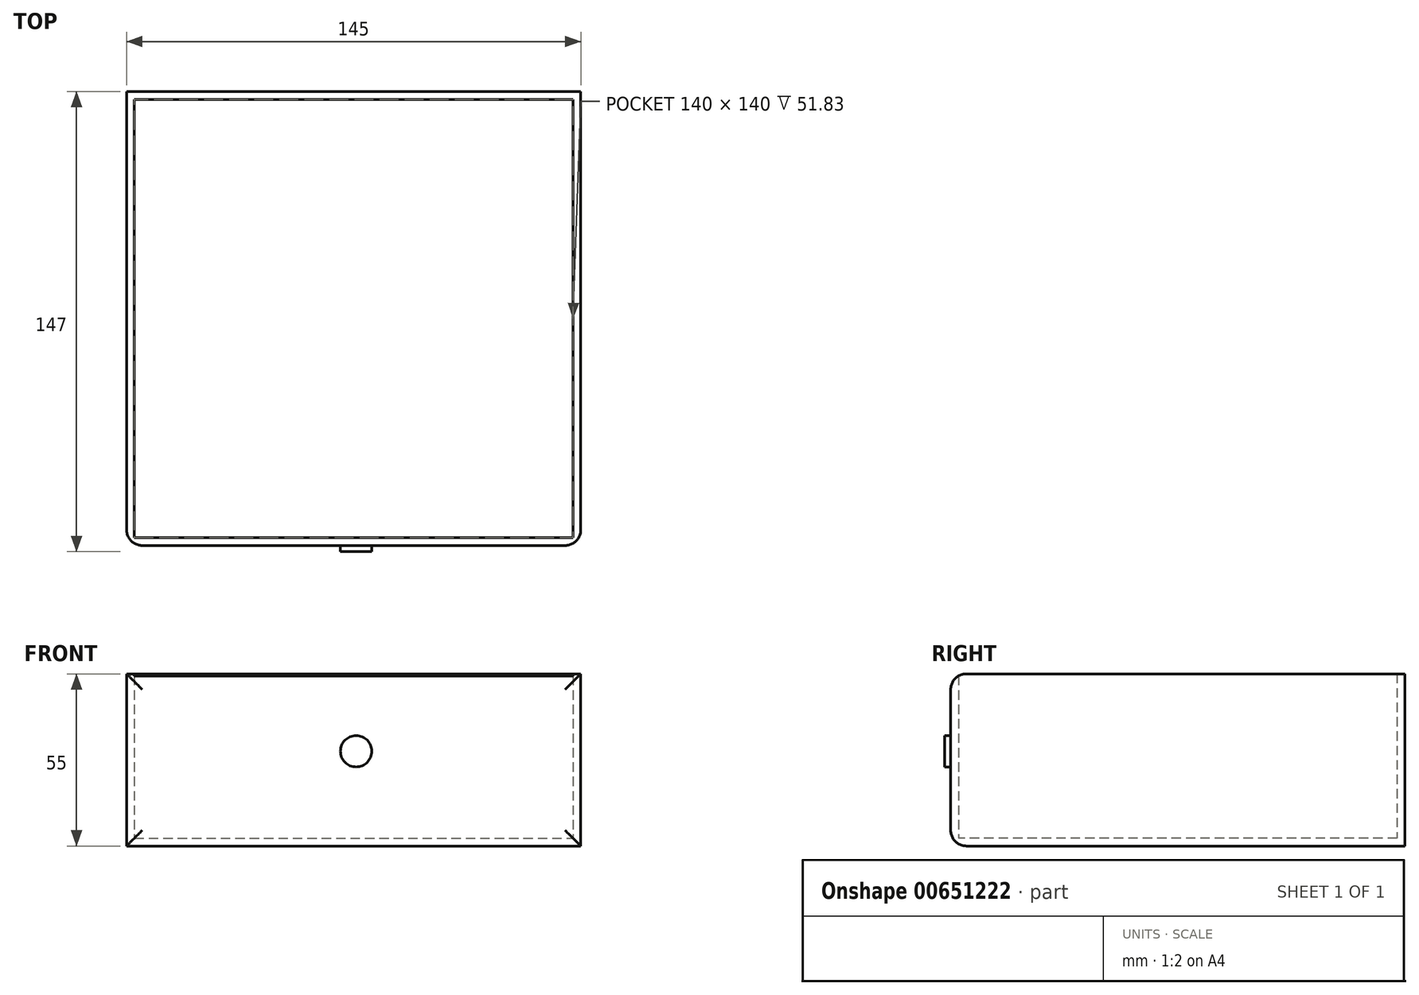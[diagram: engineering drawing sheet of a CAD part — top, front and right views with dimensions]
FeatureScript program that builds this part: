
annotation { "Feature Type Name" : "Feature", "Feature Type Description" : "" }
export const myFeature = defineFeature(function(context is Context, id is Id, definition is map)
    precondition{}
    {
        {
            var Q0;
            Q0=qCreatedBy(makeId("Top.planeOp"),FACE);
            var sketch = newSketch(context, id + "F0", { "sketchPlane" : qUnion([Q0])});
            skLineSegment(sketch, "E0.bottom", {"start": v(-73.28, 72.37) * mm, "end": v(71.72, 72.37) * mm});
            skLineSegment(sketch, "E0.top", {"start": v(-73.28, -72.63) * mm, "end": v(71.72, -72.63) * mm});
            skLineSegment(sketch, "E0.left", {"start": v(-73.28, 72.37) * mm, "end": v(-73.28, -72.63) * mm});
            skLineSegment(sketch, "E0.right", {"start": v(71.72, 72.37) * mm, "end": v(71.72, -72.63) * mm});
            skSolve(sketch);
        }
        {
            var Q0;
            Q0 = qSketchRegion(id + "F0", true);
            extrude(context, id + "F1", {"entities" : qUnion([Q0]), "depth" : 55 * mm, "offsetDistance" : 25 * mm});
        }
        {
            var Q0;
            Q0=makeQuery(id+"F1.opExtrude","CAP_FACE",FACE,{"disambiguationData":[OSD([sQuery(id+"F0.wireOp",EDGE,"E0.bottom"),sQuery(id+"F0.wireOp",EDGE,"E0.top"),sQuery(id+"F0.wireOp",EDGE,"E0.left"),sQuery(id+"F0.wireOp",EDGE,"E0.right")])],"isStart":false});
            shell(context, id + "F2", {"entities" : qUnion([Q0]), "thickness" : 2.5 * mm});
        }
        {
            var Q0;
            Q0=makeQuery(id+"F1.opExtrude","SWEPT_FACE",FACE,{"disambiguationData":[OSD([sQuery(id+"F0.wireOp",EDGE,"E0.top")])]});
            fillet(context, id + "F3", {"entities" : qUnion([Q0]), "radius" : 5 * mm, "tangentPropagation" : true, "allowEdgeOverflow" : false});
        }
        {
            var Q0;
            Q0=makeQuery(id+"F1.opExtrude","SWEPT_FACE",FACE,{"disambiguationData":[OSD([sQuery(id+"F0.wireOp",EDGE,"E0.top")])]});
            var sketch = newSketch(context, id + "F4", { "sketchPlane" : qUnion([Q0])});
            skCircle(sketch, "E1", {"center": v(0, 30.27) * mm, "radius": 5 * mm});
            skLineSegment(sketch, "E2", {"start": v(0, 35.27) * mm, "end": v(0, 25.27) * mm});
            skSolve(sketch);
        }
        {
            var Q0;
            Q0 = qSketchRegion(id + "F4", true);
            extrude(context, id + "F5", {"entities" : qUnion([Q0]), "operationType" : NewBodyOperationType.ADD, "depth" : 2 * mm, "offsetDistance" : 25 * mm});
        }
    });
